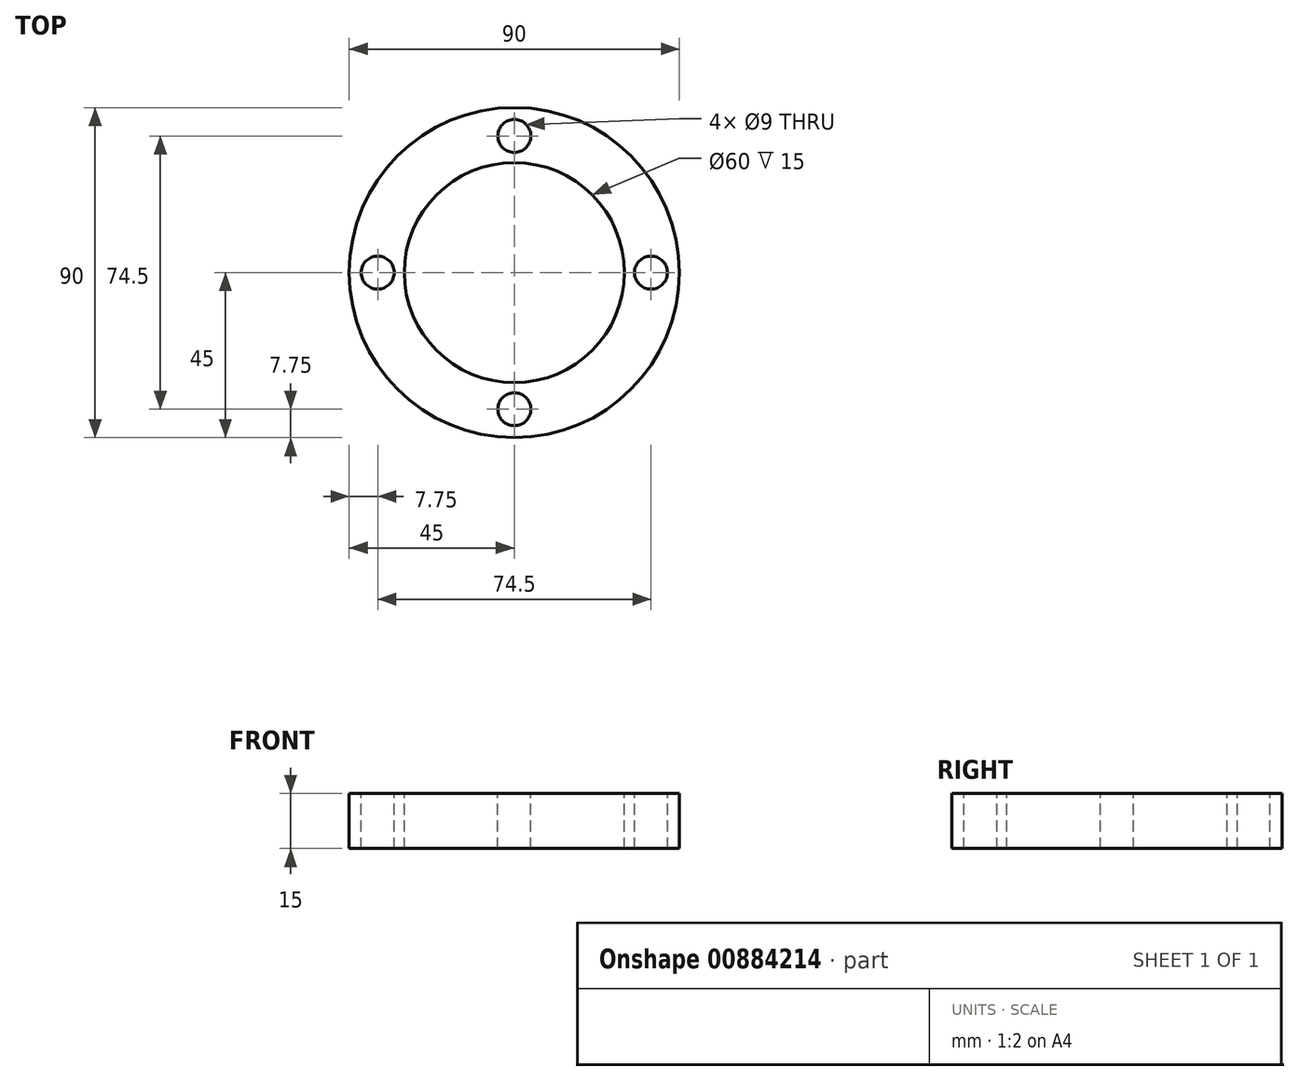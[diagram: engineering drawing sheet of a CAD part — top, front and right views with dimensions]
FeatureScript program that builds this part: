
annotation { "Feature Type Name" : "Feature", "Feature Type Description" : "" }
export const myFeature = defineFeature(function(context is Context, id is Id, definition is map)
    precondition{}
    {
        {
            var Q0;
            Q0=qCreatedBy(makeId("Top.planeOp"),FACE);
            var sketch = newSketch(context, id + "F0", { "sketchPlane" : qUnion([Q0])});
            skCircle(sketch, "E0", {"center": v(0, 0) * mm, "radius": 45 * mm});
            skSolve(sketch);
        }
        {
            var Q0;
            Q0=makeQuery(id+"F0.imprint","IMPRINT",FACE,{"disambiguationData":[TD([[makeQuery(id+"F0.imprint","IMPRINT",EDGE,{"derivedFrom":sQuery(id+"F0.wireOp",EDGE,"E0")}),1.0]])]});
            extrude(context, id + "F1", {"entities" : qUnion([Q0]), "depth" : 15 * mm, "offsetDistance" : 25 * mm});
        }
        {
            var Q0;
            Q0=makeQuery(id+"F1.opExtrude","CAP_FACE",FACE,{"disambiguationData":[OSD([sQuery(id+"F0.wireOp",EDGE,"E0")])],"isStart":false});
            var sketch = newSketch(context, id + "F2", { "sketchPlane" : qUnion([Q0])});
            skCircle(sketch, "E1", {"center": v(0, 0) * mm, "radius": 30 * mm});
            skSolve(sketch);
        }
        {
            var Q0;
            Q0=makeQuery(id+"F2.imprint","IMPRINT",FACE,{"disambiguationData":[TD([[makeQuery(id+"F2.imprint","IMPRINT",EDGE,{"derivedFrom":sQuery(id+"F2.wireOp",EDGE,"E1")}),1.0]])]});
            extrude(context, id + "F3", {"entities" : qUnion([Q0]), "operationType" : NewBodyOperationType.REMOVE, "endBound" : BoundingType.THROUGH_ALL, "oppositeDirection" : true, "depth" : 25 * mm, "offsetDistance" : 25 * mm});
        }
        {
            var Q0;
            Q0=makeQuery(id+"F1.opExtrude","CAP_FACE",FACE,{"disambiguationData":[OSD([sQuery(id+"F0.wireOp",EDGE,"E0")])],"isStart":false});
            var sketch = newSketch(context, id + "F4", { "sketchPlane" : qUnion([Q0])});
            skCircle(sketch, "E2", {"center": v(0, 0) * mm, "radius": 37.25 * mm, "construction": true});
            skCircle(sketch, "E3", {"center": v(0, 37.25) * mm, "radius": 4.5 * mm});
            skCircle(sketch, "E4", {"center": v(37.25, 0) * mm, "radius": 4.5 * mm});
            skCircle(sketch, "E5", {"center": v(-37.25, 0) * mm, "radius": 4.5 * mm});
            skCircle(sketch, "E6", {"center": v(0, -37.25) * mm, "radius": 4.5 * mm});
            skSolve(sketch);
        }
        {
            var Q0;
            Q0=makeQuery(id+"F4.imprint","IMPRINT",FACE,{"disambiguationData":[TD([[makeQuery(id+"F4.imprint","IMPRINT",EDGE,{"derivedFrom":sQuery(id+"F4.wireOp",EDGE,"E3")}),1.0]])]});
            var Q1;
            Q1=makeQuery(id+"F4.imprint","IMPRINT",FACE,{"disambiguationData":[TD([[makeQuery(id+"F4.imprint","IMPRINT",EDGE,{"derivedFrom":sQuery(id+"F4.wireOp",EDGE,"E5")}),1.0]])]});
            var Q2;
            Q2=makeQuery(id+"F4.imprint","IMPRINT",FACE,{"disambiguationData":[TD([[makeQuery(id+"F4.imprint","IMPRINT",EDGE,{"derivedFrom":sQuery(id+"F4.wireOp",EDGE,"E4")}),1.0]])]});
            var Q3;
            Q3=makeQuery(id+"F4.imprint","IMPRINT",FACE,{"disambiguationData":[TD([[makeQuery(id+"F4.imprint","IMPRINT",EDGE,{"derivedFrom":sQuery(id+"F4.wireOp",EDGE,"E6")}),1.0]])]});
            extrude(context, id + "F5", {"entities" : qUnion([Q0, Q1, Q2, Q3]), "operationType" : NewBodyOperationType.REMOVE, "endBound" : BoundingType.THROUGH_ALL, "oppositeDirection" : true, "depth" : 25 * mm, "offsetDistance" : 25 * mm});
        }
    });
